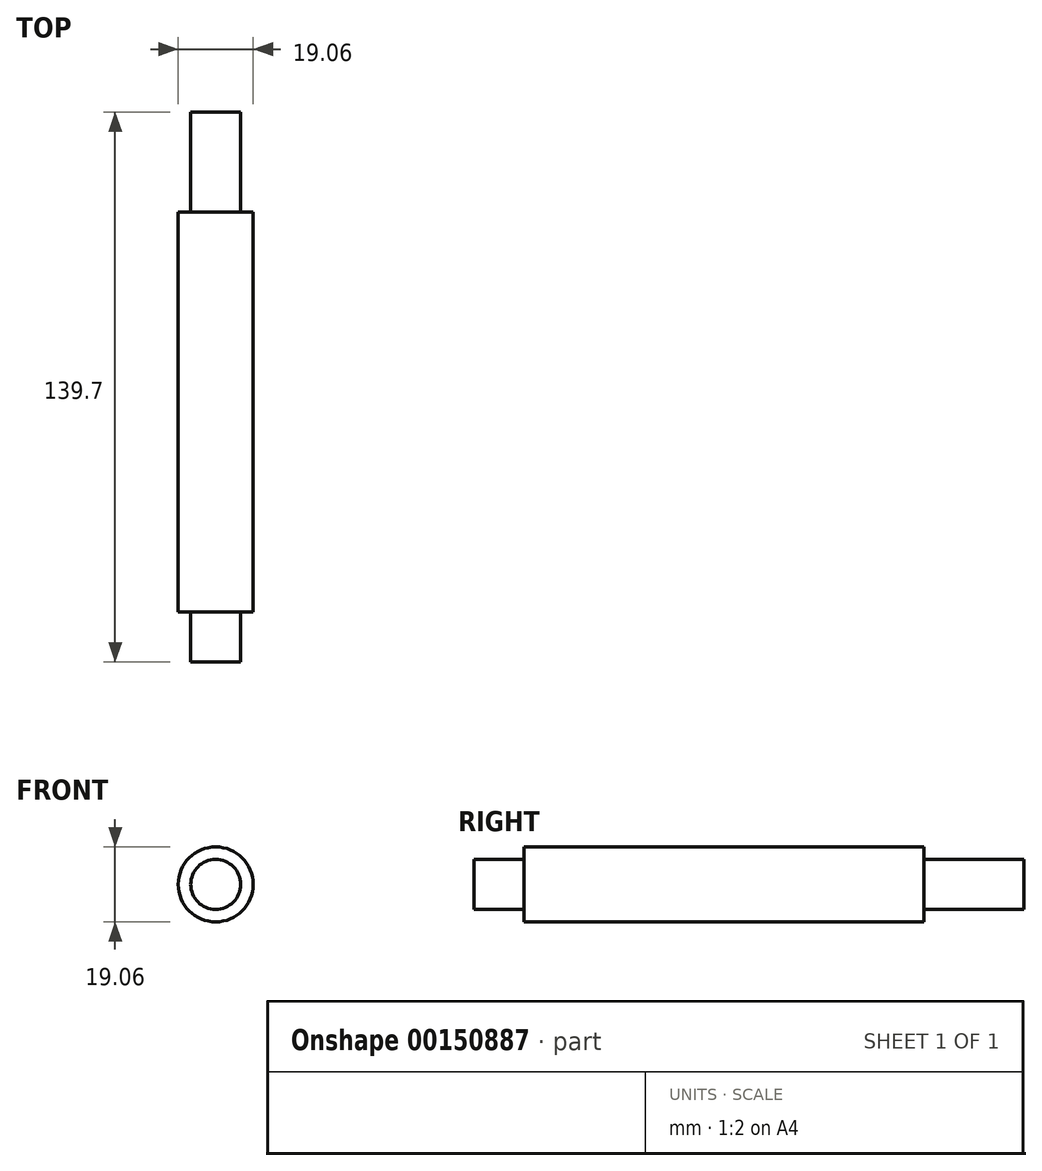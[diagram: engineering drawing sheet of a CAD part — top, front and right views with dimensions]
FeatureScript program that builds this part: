
annotation { "Feature Type Name" : "Feature", "Feature Type Description" : "" }
export const myFeature = defineFeature(function(context is Context, id is Id, definition is map)
    precondition{}
    {
        {
            var Q0;
            Q0=qCreatedBy(makeId("Front.planeOp"),FACE);
            var sketch = newSketch(context, id + "F0", { "sketchPlane" : qUnion([Q0])});
            skCircle(sketch, "E0", {"center": v(0, 0) * mm, "radius": 9.53 * mm});
            skSolve(sketch);
        }
        {
            var Q0;
            Q0 = qSketchRegion(id + "F0", true);
            extrude(context, id + "F1", {"entities" : qUnion([Q0]), "depth" : 101.6 * mm});
        }
        {
            var Q0;
            Q0=makeQuery(id+"F1.opExtrude","CAP_FACE",FACE,{"disambiguationData":[OSD([sQuery(id+"F0.wireOp",EDGE,"E0")])],"isStart":false});
            var sketch = newSketch(context, id + "F2", { "sketchPlane" : qUnion([Q0])});
            skCircle(sketch, "E1", {"center": v(0, 0) * mm, "radius": 6.35 * mm});
            skSolve(sketch);
        }
        {
            var Q0;
            Q0 = qSketchRegion(id + "F2", true);
            extrude(context, id + "F3", {"entities" : qUnion([Q0]), "operationType" : NewBodyOperationType.ADD, "depth" : 12.7 * mm});
        }
        {
            var Q0;
            Q0=qCreatedBy(makeId("Front.planeOp"),FACE);
            var sketch = newSketch(context, id + "F4", { "sketchPlane" : qUnion([Q0])});
            skCircle(sketch, "E2", {"center": v(0, 0) * mm, "radius": 6.35 * mm});
            skSolve(sketch);
        }
        {
            var Q0;
            Q0 = qSketchRegion(id + "F4", true);
            extrude(context, id + "F5", {"entities" : qUnion([Q0]), "operationType" : NewBodyOperationType.ADD, "oppositeDirection" : true, "depth" : 25.4 * mm});
        }
    });
